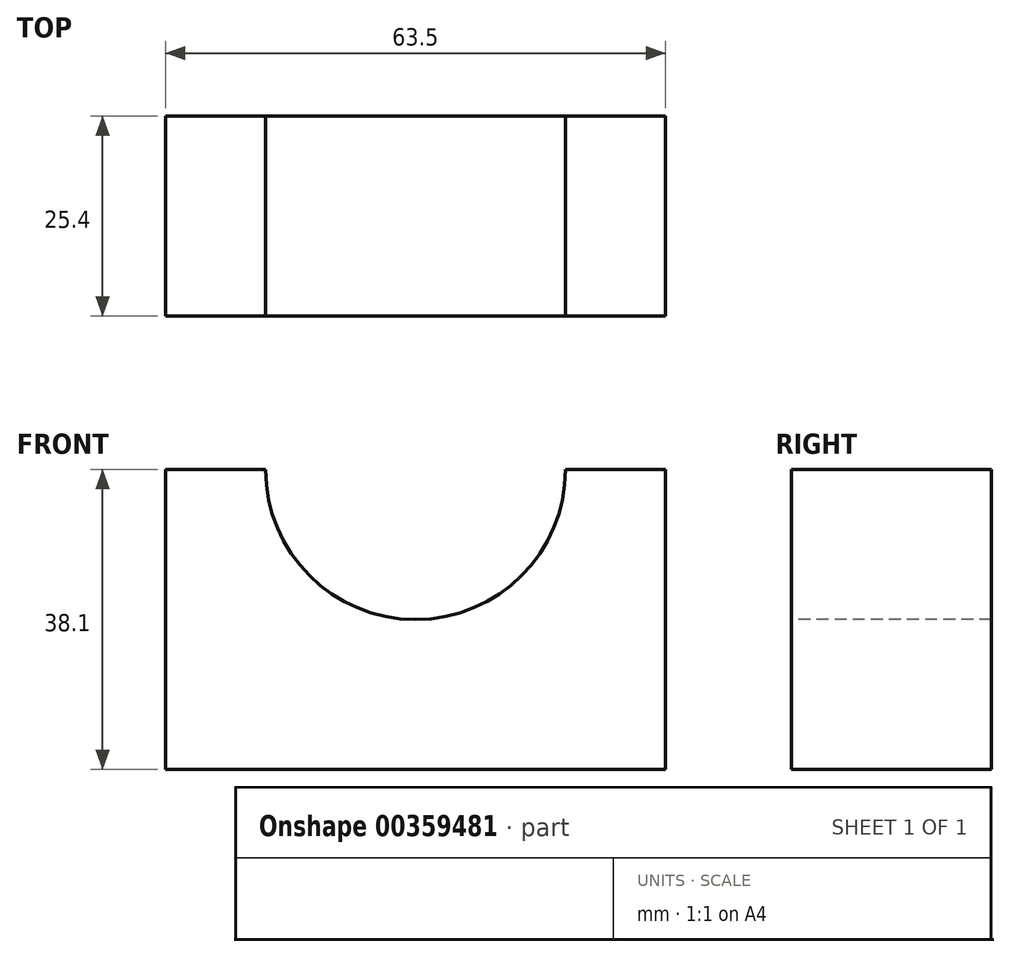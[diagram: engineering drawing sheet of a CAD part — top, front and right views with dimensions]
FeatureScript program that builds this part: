
annotation { "Feature Type Name" : "Feature", "Feature Type Description" : "" }
export const myFeature = defineFeature(function(context is Context, id is Id, definition is map)
    precondition{}
    {
        {
            var Q0;
            Q0=qCreatedBy(makeId("Front.planeOp"),FACE);
            var sketch = newSketch(context, id + "F0", { "sketchPlane" : qUnion([Q0])});
            skLineSegment(sketch, "E0", {"start": v(0, 38.1) * mm, "end": v(0, 0) * mm});
            skLineSegment(sketch, "E1", {"start": v(0, 0) * mm, "end": v(63.5, 0) * mm});
            skLineSegment(sketch, "E2", {"start": v(63.5, 0) * mm, "end": v(63.5, 38.1) * mm});
            skLineSegment(sketch, "E3", {"start": v(63.5, 38.1) * mm, "end": v(0, 38.1) * mm});
            skSolve(sketch);
        }
        {
            var Q0;
            Q0 = qSketchRegion(id + "F0", true);
            extrude(context, id + "F1", {"entities" : qUnion([Q0]), "oppositeDirection" : true, "depth" : 25.4 * mm});
        }
        {
            var Q0;
            Q0=qCreatedBy(makeId("Front.planeOp"),FACE);
            var sketch = newSketch(context, id + "F2", { "sketchPlane" : qUnion([Q0])});
            skArc(sketch, "E4", {"start": v(12.7, 38.1) * mm, "mid": v(31.75, 19.05) * mm, "end": v(50.8, 38.1) * mm});
            skLineSegment(sketch, "E5", {"start": v(12.7, 38.1) * mm, "end": v(50.8, 38.1) * mm});
            skSolve(sketch);
        }
        {
            var Q0;
            Q0 = qSketchRegion(id + "F2", true);
            extrude(context, id + "F3", {"entities" : qUnion([Q0]), "operationType" : NewBodyOperationType.REMOVE, "oppositeDirection" : true, "depth" : 25.4 * mm});
        }
    });
